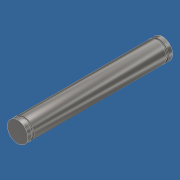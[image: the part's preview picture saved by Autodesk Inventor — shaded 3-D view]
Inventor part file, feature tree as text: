
AUTODESK INVENTOR PART (.ipt)
format: ipt  version: 2018 (Build 220112000, 112)  size: 129,024 bytes
history: native  units: mm
features: extrude x2, sketch x2, revolve x1, plane x1
ambient origin geometry x8: Origin, YZ Plane, XZ Plane, XY Plane, X Axis, Y Axis, Z Axis, Center Point
bodies: Solid1 (feature_tree)
feature tree (6):
  extrude  "Extrusion1"  Depth=56.5mm TaperAngle=0.0deg
  revolve  "Revolution1"  [1 undecoded]
  plane  "Work Plane1"
  extrude  "Extrusion4"  Depth=2.0mm
  sketch  "Sketch2"  dims[d0=8.0mm d2=56.5mm d3=0.0mm]
  sketch  "Sketch5"  dims[d9=0.94mm d10=0.5mm d11=3.0mm d12=1.5mm d13=90.0deg d19=2.0mm d20=3.0mm d23=18.0mm d25=14.0mm d27=1.2mm d28=0.0mm]
note: 1 required parameter value undecoded (feature->parameter linkage not recoverable at this tier; creation-order binding heuristic only, values carry confidence <= 0.55)
